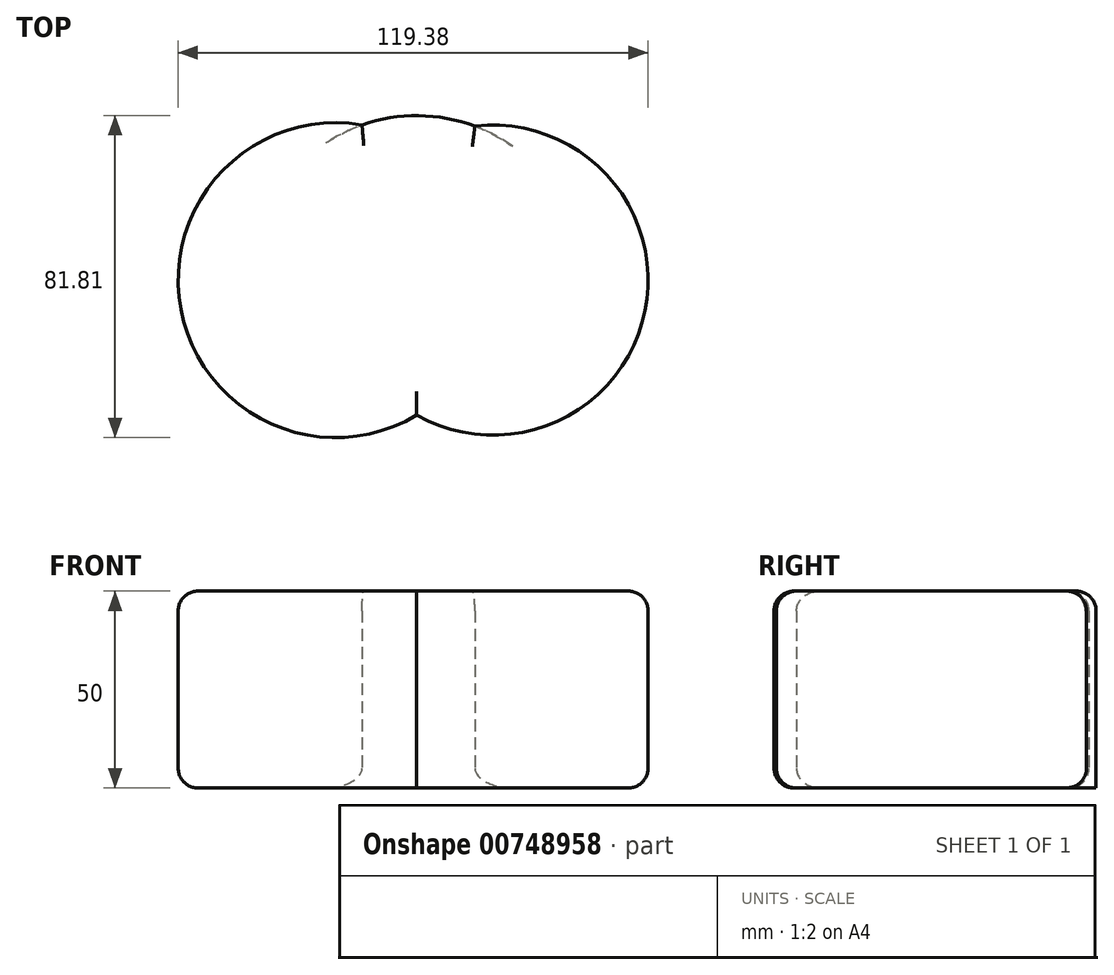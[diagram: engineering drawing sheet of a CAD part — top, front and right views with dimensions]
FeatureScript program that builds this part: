
annotation { "Feature Type Name" : "Feature", "Feature Type Description" : "" }
export const myFeature = defineFeature(function(context is Context, id is Id, definition is map)
    precondition{}
    {
        {
            var Q0;
            Q0=qCreatedBy(makeId("Top.planeOp"),FACE);
            var sketch = newSketch(context, id + "F0", { "sketchPlane" : qUnion([Q0])});
            skCircle(sketch, "E0", {"center": v(0, 0) * mm, "radius": 41.81 * mm});
            skCircle(sketch, "E1", {"center": v(-20.62, 0) * mm, "radius": 40 * mm});
            skCircle(sketch, "E2", {"center": v(19.38, 0) * mm, "radius": 39.39 * mm});
            skSolve(sketch);
        }
        {
            var Q0;
            {var subQ0=sQuery(id+"F0.wireOp",EDGE,"E1");var subQ1=sQuery(id+"F0.wireOp",EDGE,"E0");var subQ2=makeQuery(id+"F0.imprint","INTERSECT",VERTEX,{"disambiguationData":[OD(0.0)],"derivedFrom":[subQ1,subQ0]});Q0=makeQuery(id+"F0.imprint","IMPRINT",FACE,{"disambiguationData":[TD([[makeQuery(id+"F0.imprint","IMPRINT",EDGE,{"disambiguationData":[TD([[subQ2,-1.0]])],"derivedFrom":subQ1}),-1.0]])]});}
            var Q1;
            {var subQ0=sQuery(id+"F0.wireOp",EDGE,"E1");var subQ1=sQuery(id+"F0.wireOp",EDGE,"E0");var subQ2=makeQuery(id+"F0.imprint","INTERSECT",VERTEX,{"disambiguationData":[OD(0.0)],"derivedFrom":[subQ1,subQ0]});Q1=makeQuery(id+"F0.imprint","IMPRINT",FACE,{"disambiguationData":[TD([[makeQuery(id+"F0.imprint","IMPRINT",EDGE,{"disambiguationData":[TD([[subQ2,-1.0]])],"derivedFrom":subQ1}),1.0]])]});}
            var Q2;
            {var subQ0=sQuery(id+"F0.wireOp",EDGE,"E2");var subQ1=sQuery(id+"F0.wireOp",EDGE,"E1");var subQ2=makeQuery(id+"F0.imprint","INTERSECT",VERTEX,{"disambiguationData":[OD(0.0)],"derivedFrom":[subQ1,subQ0]});Q2=makeQuery(id+"F0.imprint","IMPRINT",FACE,{"disambiguationData":[TD([[makeQuery(id+"F0.imprint","IMPRINT",EDGE,{"disambiguationData":[TD([[subQ2,1.0]])],"derivedFrom":subQ1}),1.0]])]});}
            var Q3;
            {var subQ0=sQuery(id+"F0.wireOp",EDGE,"E2");var subQ1=sQuery(id+"F0.wireOp",EDGE,"E0");var subQ2=makeQuery(id+"F0.imprint","INTERSECT",VERTEX,{"disambiguationData":[OD(0.0)],"derivedFrom":[subQ1,subQ0]});Q3=makeQuery(id+"F0.imprint","IMPRINT",FACE,{"disambiguationData":[TD([[makeQuery(id+"F0.imprint","IMPRINT",EDGE,{"disambiguationData":[TD([[subQ2,1.0]])],"derivedFrom":subQ1}),1.0]])]});}
            var Q4;
            {var subQ0=sQuery(id+"F0.wireOp",EDGE,"E2");var subQ1=sQuery(id+"F0.wireOp",EDGE,"E0");var subQ2=makeQuery(id+"F0.imprint","INTERSECT",VERTEX,{"disambiguationData":[OD(0.0)],"derivedFrom":[subQ1,subQ0]});Q4=makeQuery(id+"F0.imprint","IMPRINT",FACE,{"disambiguationData":[TD([[makeQuery(id+"F0.imprint","IMPRINT",EDGE,{"disambiguationData":[TD([[subQ2,1.0]])],"derivedFrom":subQ1}),-1.0]])]});}
            var Q5;
            {var subQ0=sQuery(id+"F0.wireOp",EDGE,"E1");var subQ1=sQuery(id+"F0.wireOp",EDGE,"E0");var subQ2=makeQuery(id+"F0.imprint","INTERSECT",VERTEX,{"disambiguationData":[OD(0.0)],"derivedFrom":[subQ1,subQ0]});Q5=makeQuery(id+"F0.imprint","IMPRINT",FACE,{"disambiguationData":[TD([[makeQuery(id+"F0.imprint","IMPRINT",EDGE,{"disambiguationData":[TD([[subQ2,1.0]])],"derivedFrom":subQ1}),1.0]])]});}
            extrude(context, id + "F1", {"entities" : qUnion([Q0, Q1, Q2, Q3, Q4, Q5]), "depth" : 25 * mm, "offsetDistance" : 25 * mm});
        }
        {
            var Q0;
            Q0=makeQuery(id+"F1.opExtrude","CAP_FACE",FACE,{"disambiguationData":[OSD([sQuery(id+"F0.wireOp",EDGE,"E0"),sQuery(id+"F0.wireOp",EDGE,"E1"),sQuery(id+"F0.wireOp",EDGE,"E2")])],"isStart":false});
            extrude(context, id + "F2", {"entities" : qUnion([Q0]), "operationType" : NewBodyOperationType.ADD, "depth" : 25 * mm, "offsetDistance" : 25 * mm});
        }
        {
            var Q0;
            Q0=makeQuery(id+"F2.opExtrude","CAP_EDGE",EDGE,{"disambiguationData":[OSD([sQuery(id+"F0.wireOp",EDGE,"E2")])],"isStart":false});
            var Q1;
            Q1=makeQuery(id+"F2.opExtrude","CAP_FACE",FACE,{"disambiguationData":[OSD([sQuery(id+"F0.wireOp",EDGE,"E0"),sQuery(id+"F0.wireOp",EDGE,"E1"),sQuery(id+"F0.wireOp",EDGE,"E2")])],"isStart":false});
            var Q2;
            Q2=makeQuery(id+"F1.opExtrude","CAP_EDGE",EDGE,{"disambiguationData":[OSD([sQuery(id+"F0.wireOp",EDGE,"E1")])],"isStart":true});
            var Q3;
            Q3=makeQuery(id+"F1.opExtrude","CAP_EDGE",EDGE,{"disambiguationData":[OSD([sQuery(id+"F0.wireOp",EDGE,"E2")])],"isStart":true});
            fillet(context, id + "F3", {"entities" : qUnion([Q0, Q1, Q2, Q3]), "radius" : 5 * mm, "tangentPropagation" : true, "allowEdgeOverflow" : false});
        }
    });
